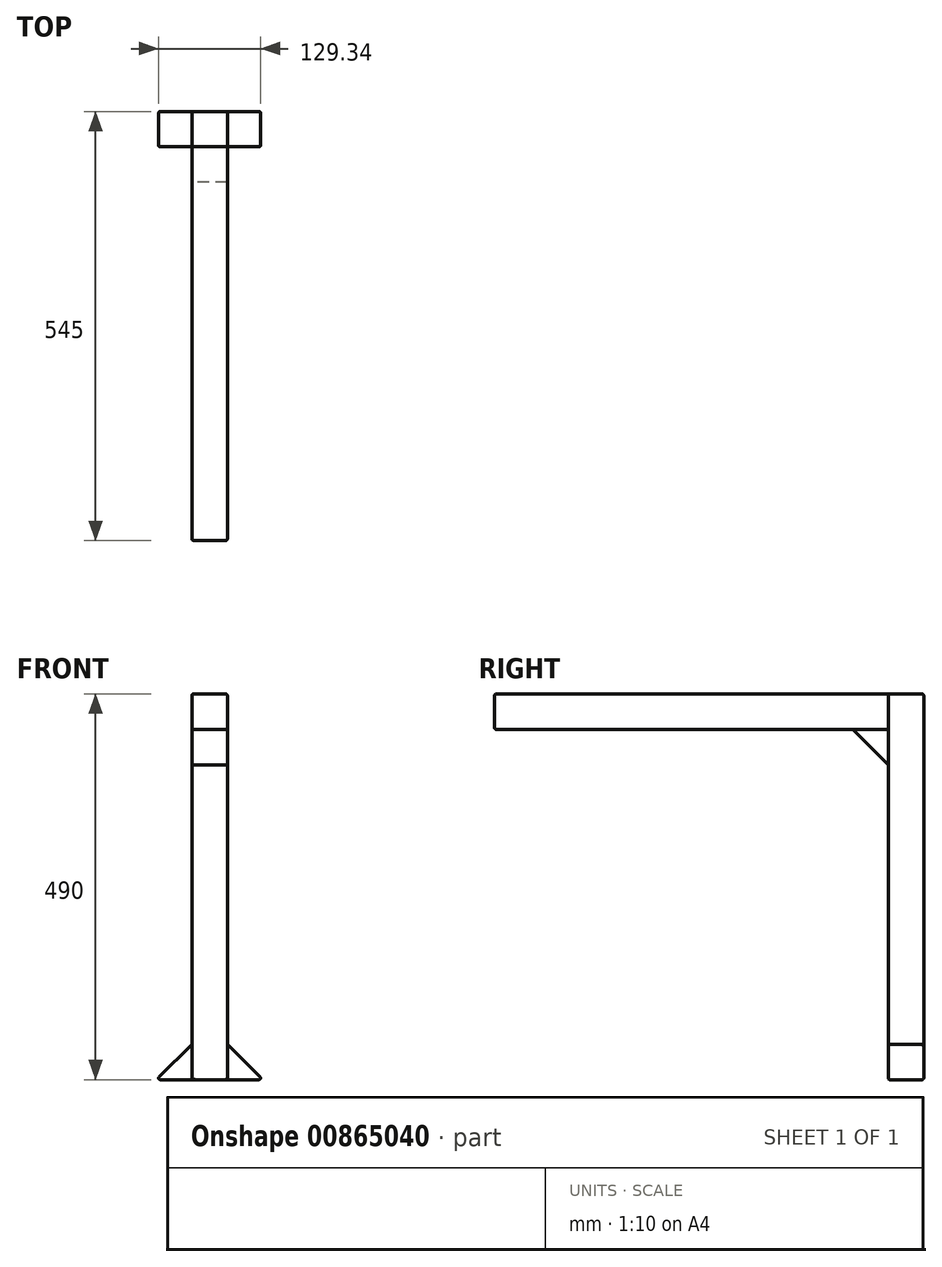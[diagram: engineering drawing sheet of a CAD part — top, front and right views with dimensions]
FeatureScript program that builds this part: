
annotation { "Feature Type Name" : "Feature", "Feature Type Description" : "" }
export const myFeature = defineFeature(function(context is Context, id is Id, definition is map)
    precondition{}
    {
        {
            var Q0;
            Q0=qCreatedBy(makeId("Top.planeOp"),FACE);
            var sketch = newSketch(context, id + "F0", { "sketchPlane" : qUnion([Q0])});
            skLineSegment(sketch, "E0.bottom", {"start": v(0, 0) * mm, "end": v(45, 0) * mm});
            skLineSegment(sketch, "E0.top", {"start": v(0, 45) * mm, "end": v(45, 45) * mm});
            skLineSegment(sketch, "E0.left", {"start": v(0, 0) * mm, "end": v(0, 45) * mm});
            skLineSegment(sketch, "E0.right", {"start": v(45, 0) * mm, "end": v(45, 45) * mm});
            skSolve(sketch);
        }
        {
            var Q0;
            Q0=makeQuery(id+"F0.imprint","IMPRINT",FACE,{"disambiguationData":[TD([[makeQuery(id+"F0.imprint","IMPRINT",EDGE,{"derivedFrom":sQuery(id+"F0.wireOp",EDGE,"E0.bottom")}),1.0]])]});
            extrude(context, id + "F1", {"entities" : qUnion([Q0]), "depth" : 490 * mm, "offsetDistance" : 25 * mm});
        }
        {
            var Q0;
            Q0=qCreatedBy(makeId("Front.planeOp"),FACE);
            var sketch = newSketch(context, id + "F2", { "sketchPlane" : qUnion([Q0])});
            skLineSegment(sketch, "E1.bottom", {"start": v(45, 0) * mm, "end": v(90, 0) * mm});
            skLineSegment(sketch, "E1.left", {"start": v(45, 0) * mm, "end": v(45, 45) * mm});
            skLineSegment(sketch, "E2", {"start": v(45, 45) * mm, "end": v(90, 0) * mm});
            skLineSegment(sketch, "E3", {"start": v(22.5, 0) * mm, "end": v(22.5, 61.67) * mm, "construction": true});
            skLineSegment(sketch, "E4.MirrorCS", {"start": v(0, 45) * mm, "end": v(-45, 0) * mm});
            skLineSegment(sketch, "E5.MirrorCS", {"start": v(0, 0) * mm, "end": v(0, 45) * mm});
            skLineSegment(sketch, "E6.MirrorCS", {"start": v(0, 0) * mm, "end": v(-45, 0) * mm});
            skSolve(sketch);
        }
        {
            var Q0;
            Q0=makeQuery(id+"F2.imprint","IMPRINT",FACE,{"disambiguationData":[TD([[makeQuery(id+"F2.imprint","IMPRINT",EDGE,{"derivedFrom":sQuery(id+"F2.wireOp",EDGE,"E4.MirrorCS")}),1.0]])]});
            var Q1;
            Q1=makeQuery(id+"F2.imprint","IMPRINT",FACE,{"disambiguationData":[TD([[makeQuery(id+"F2.imprint","IMPRINT",EDGE,{"derivedFrom":sQuery(id+"F2.wireOp",EDGE,"E1.bottom")}),1.0]])]});
            extrude(context, id + "F3", {"entities" : qUnion([Q0, Q1]), "oppositeDirection" : true, "depth" : 45 * mm, "offsetDistance" : 25 * mm});
        }
        {
            var Q0;
            Q0=makeQuery(id+"F1.opExtrude","SWEPT_FACE",FACE,{"disambiguationData":[OSD([sQuery(id+"F0.wireOp",EDGE,"E0.bottom")])]});
            var sketch = newSketch(context, id + "F4", { "sketchPlane" : qUnion([Q0])});
            skLineSegment(sketch, "E7.bottom", {"start": v(0, 490) * mm, "end": v(45, 490) * mm});
            skLineSegment(sketch, "E7.top", {"start": v(0, 445) * mm, "end": v(45, 445) * mm});
            skLineSegment(sketch, "E7.left", {"start": v(0, 490) * mm, "end": v(0, 445) * mm});
            skLineSegment(sketch, "E7.right", {"start": v(45, 490) * mm, "end": v(45, 445) * mm});
            skSolve(sketch);
        }
        {
            var Q0;
            Q0=makeQuery(id+"F4.imprint","IMPRINT",FACE,{"disambiguationData":[TD([[makeQuery(id+"F4.imprint","IMPRINT",EDGE,{"derivedFrom":sQuery(id+"F4.wireOp",EDGE,"E7.bottom")}),-1.0]])]});
            extrude(context, id + "F5", {"entities" : qUnion([Q0]), "depth" : 500 * mm, "offsetDistance" : 25 * mm});
        }
        {
            var Q0;
            Q0=makeQuery(id+"F5.opExtrude","SWEPT_EDGE",EDGE,{"disambiguationData":[OSD([sQuery(id+"F4.wireOp",EDGE,"E7.bottom"),sQuery(id+"F4.wireOp",EDGE,"E7.left")])]});
            var Q1;
            Q1=makeQuery(id+"F5.opExtrude","SWEPT_EDGE",EDGE,{"disambiguationData":[OSD([sQuery(id+"F4.wireOp",EDGE,"E7.bottom"),sQuery(id+"F4.wireOp",EDGE,"E7.right")])]});
            var Q2;
            Q2=makeQuery(id+"F5.opExtrude","SWEPT_EDGE",EDGE,{"disambiguationData":[OSD([sQuery(id+"F0.wireOp",EDGE,"E0.bottom"),sQuery(id+"F0.wireOp",EDGE,"E0.left"),sQuery(id+"F4.wireOp",EDGE,"E7.top"),sQuery(id+"F4.wireOp",EDGE,"E7.left")])]});
            var Q3;
            Q3=makeQuery(id+"F5.opExtrude","CAP_EDGE",EDGE,{"disambiguationData":[OSD([sQuery(id+"F4.wireOp",EDGE,"E7.left")])],"isStart":false});
            var Q4;
            Q4=makeQuery(id+"F5.opExtrude","CAP_EDGE",EDGE,{"disambiguationData":[OSD([sQuery(id+"F4.wireOp",EDGE,"E7.bottom")])],"isStart":false});
            var Q5;
            Q5=makeQuery(id+"F5.opExtrude","CAP_EDGE",EDGE,{"disambiguationData":[OSD([sQuery(id+"F4.wireOp",EDGE,"E7.right")])],"isStart":false});
            var Q6;
            Q6=makeQuery(id+"F5.opExtrude","CAP_EDGE",EDGE,{"disambiguationData":[OSD([sQuery(id+"F4.wireOp",EDGE,"E7.top")])],"isStart":false});
            var Q7;
            Q7=makeQuery(id+"F5.opExtrude","SWEPT_EDGE",EDGE,{"disambiguationData":[OSD([sQuery(id+"F0.wireOp",EDGE,"E0.bottom"),sQuery(id+"F0.wireOp",EDGE,"E0.right"),sQuery(id+"F4.wireOp",EDGE,"E7.top"),sQuery(id+"F4.wireOp",EDGE,"E7.right")])]});
            var Q8;
            Q8=makeQuery(id+"F1.opExtrude","SWEPT_EDGE",EDGE,{"disambiguationData":[OSD([sQuery(id+"F0.wireOp",EDGE,"E0.bottom"),sQuery(id+"F0.wireOp",EDGE,"E0.right")])]});
            var Q9;
            Q9=makeQuery(id+"F1.opExtrude","SWEPT_EDGE",EDGE,{"disambiguationData":[OSD([sQuery(id+"F0.wireOp",EDGE,"E0.top"),sQuery(id+"F0.wireOp",EDGE,"E0.right")])]});
            var Q10;
            Q10=makeQuery(id+"F1.opExtrude","CAP_EDGE",EDGE,{"disambiguationData":[OSD([sQuery(id+"F0.wireOp",EDGE,"E0.right")])],"isStart":false});
            var Q11;
            Q11=makeQuery(id+"F1.opExtrude","CAP_EDGE",EDGE,{"disambiguationData":[OSD([sQuery(id+"F0.wireOp",EDGE,"E0.bottom")])],"isStart":false});
            var Q12;
            Q12=makeQuery(id+"F1.opExtrude","CAP_EDGE",EDGE,{"disambiguationData":[OSD([sQuery(id+"F0.wireOp",EDGE,"E0.left")])],"isStart":false});
            var Q13;
            Q13=makeQuery(id+"F1.opExtrude","CAP_EDGE",EDGE,{"disambiguationData":[OSD([sQuery(id+"F0.wireOp",EDGE,"E0.top")])],"isStart":false});
            var Q14;
            Q14=makeQuery(id+"F1.opExtrude","SWEPT_EDGE",EDGE,{"disambiguationData":[OSD([sQuery(id+"F0.wireOp",EDGE,"E0.bottom"),sQuery(id+"F0.wireOp",EDGE,"E0.left")])]});
            var Q15;
            Q15=makeQuery(id+"F1.opExtrude","SWEPT_EDGE",EDGE,{"disambiguationData":[OSD([sQuery(id+"F0.wireOp",EDGE,"E0.top"),sQuery(id+"F0.wireOp",EDGE,"E0.left")])]});
            var Q16;
            Q16=makeQuery(id+"F1.opExtrude","CAP_EDGE",EDGE,{"disambiguationData":[OSD([sQuery(id+"F0.wireOp",EDGE,"E0.bottom")])],"isStart":true});
            var Q17;
            Q17=makeQuery(id+"F3.opExtrude","CAP_EDGE",EDGE,{"disambiguationData":[OSD([sQuery(id+"F2.wireOp",EDGE,"E4.MirrorCS")])],"isStart":true});
            var Q18;
            Q18=makeQuery(id+"F3.opExtrude","CAP_EDGE",EDGE,{"disambiguationData":[OSD([sQuery(id+"F2.wireOp",EDGE,"E6.MirrorCS")])],"isStart":true});
            var Q19;
            Q19=makeQuery(id+"F3.opExtrude","SWEPT_EDGE",EDGE,{"disambiguationData":[OSD([sQuery(id+"F2.wireOp",EDGE,"E4.MirrorCS"),sQuery(id+"F2.wireOp",EDGE,"E6.MirrorCS")])]});
            var Q20;
            Q20=makeQuery(id+"F3.opExtrude","CAP_EDGE",EDGE,{"disambiguationData":[OSD([sQuery(id+"F2.wireOp",EDGE,"E4.MirrorCS")])],"isStart":false});
            var Q21;
            Q21=makeQuery(id+"F3.opExtrude","CAP_EDGE",EDGE,{"disambiguationData":[OSD([sQuery(id+"F2.wireOp",EDGE,"E1.bottom")])],"isStart":true});
            var Q22;
            Q22=makeQuery(id+"F3.opExtrude","CAP_EDGE",EDGE,{"disambiguationData":[OSD([sQuery(id+"F2.wireOp",EDGE,"E2")])],"isStart":true});
            var Q23;
            Q23=makeQuery(id+"F3.opExtrude","CAP_EDGE",EDGE,{"disambiguationData":[OSD([sQuery(id+"F2.wireOp",EDGE,"E2")])],"isStart":false});
            var Q24;
            Q24=makeQuery(id+"F3.opExtrude","CAP_EDGE",EDGE,{"disambiguationData":[OSD([sQuery(id+"F2.wireOp",EDGE,"E1.bottom")])],"isStart":false});
            var Q25;
            Q25=makeQuery(id+"F1.opExtrude","CAP_EDGE",EDGE,{"disambiguationData":[OSD([sQuery(id+"F0.wireOp",EDGE,"E0.top")])],"isStart":true});
            var Q26;
            Q26=makeQuery(id+"F3.opExtrude","CAP_EDGE",EDGE,{"disambiguationData":[OSD([sQuery(id+"F2.wireOp",EDGE,"E6.MirrorCS")])],"isStart":false});
            var Q27;
            Q27=makeQuery(id+"F3.opExtrude","SWEPT_EDGE",EDGE,{"disambiguationData":[OSD([sQuery(id+"F2.wireOp",EDGE,"E1.bottom"),sQuery(id+"F2.wireOp",EDGE,"E2")])]});
            fillet(context, id + "F6", {"entities" : qUnion([Q0, Q1, Q2, Q3, Q4, Q5, Q6, Q7, Q8, Q9, Q10, Q11, Q12, Q13, Q14, Q15, Q16, Q17, Q18, Q19, Q20, Q21, Q22, Q23, Q24, Q25, Q26, Q27]), "radius" : 2 * mm, "tangentPropagation" : true, "allowEdgeOverflow" : false});
        }
        {
            var Q0;
            Q0=makeQuery(id+"F1.opExtrude","SWEPT_FACE",FACE,{"disambiguationData":[OSD([sQuery(id+"F0.wireOp",EDGE,"E0.left")])]});
            var sketch = newSketch(context, id + "F7", { "sketchPlane" : qUnion([Q0])});
            skLineSegment(sketch, "E8.bottom", {"start": v(0, 445) * mm, "end": v(45, 445) * mm});
            skLineSegment(sketch, "E8.left", {"start": v(0, 445) * mm, "end": v(0, 400) * mm});
            skLineSegment(sketch, "E9", {"start": v(0, 400) * mm, "end": v(45, 445) * mm});
            skSolve(sketch);
        }
        {
            var Q0;
            Q0=makeQuery(id+"F7.imprint","IMPRINT",FACE,{"disambiguationData":[TD([[makeQuery(id+"F7.imprint","IMPRINT",EDGE,{"derivedFrom":sQuery(id+"F7.wireOp",EDGE,"E8.bottom")}),-1.0]])]});
            extrude(context, id + "F8", {"entities" : qUnion([Q0]), "oppositeDirection" : true, "depth" : 45 * mm, "offsetDistance" : 25 * mm});
        }
    });
